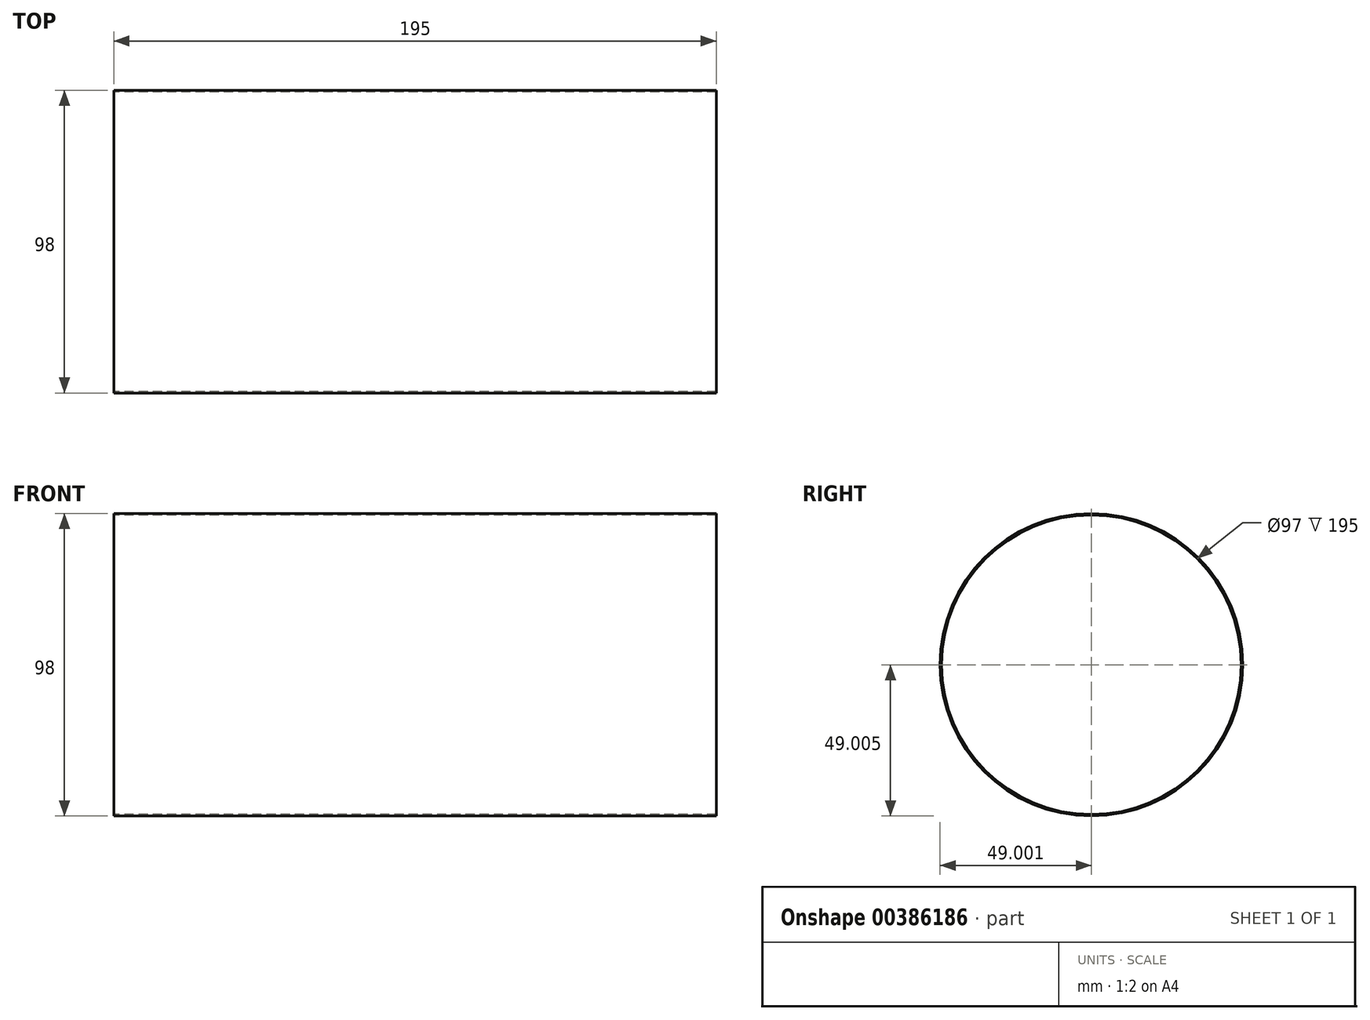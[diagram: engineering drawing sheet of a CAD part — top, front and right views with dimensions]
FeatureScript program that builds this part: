
annotation { "Feature Type Name" : "Feature", "Feature Type Description" : "" }
export const myFeature = defineFeature(function(context is Context, id is Id, definition is map)
    precondition{}
    {
        {
            var Q0;
            Q0=qCreatedBy(makeId("Right.planeOp"),FACE);
            var sketch = newSketch(context, id + "F0", { "sketchPlane" : qUnion([Q0])});
            skCircle(sketch, "E0", {"center": v(-6.13, 8.92) * mm, "radius": 49 * mm});
            skCircle(sketch, "E1", {"center": v(-6.13, 8.92) * mm, "radius": 48.5 * mm});
            skSolve(sketch);
        }
        {
            var Q0;
            Q0=makeQuery(id+"F0.imprint","IMPRINT",FACE,{"disambiguationData":[TD([[makeQuery(id+"F0.imprint","IMPRINT",EDGE,{"derivedFrom":sQuery(id+"F0.wireOp",EDGE,"E0")}),1.0]])]});
            extrude(context, id + "F1", {"entities" : qUnion([Q0]), "depth" : 195 * mm});
        }
    });
